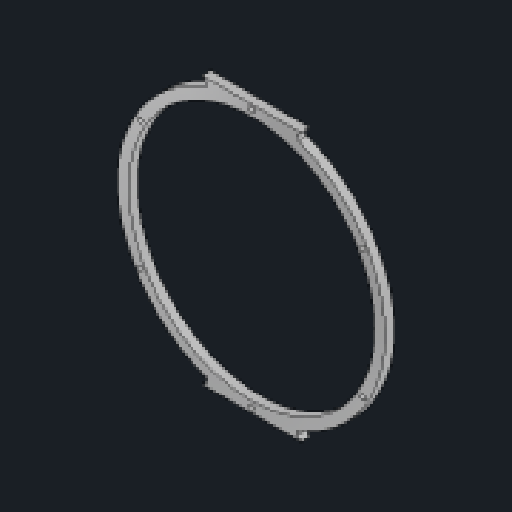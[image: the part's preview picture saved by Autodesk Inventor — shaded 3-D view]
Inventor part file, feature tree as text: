
AUTODESK INVENTOR PART (.ipt)
format: ipt  version: 2023.2 (Build 272271030, 271C)  size: 153,600 bytes
history: native  units: mm
features: extrude x4, sketch x3, mirror x2, fillet x1, pattern_circular x1
ambient origin geometry x8: Origin, YZ Plane, XZ Plane, XY Plane, X Axis, Y Axis, Z Axis, Center Point
bodies: Solid1 (feature_tree)
feature tree (11):
  sketch  "Sketch1"  dims[d0=138.0mm d1=150.0mm]
  extrude  "Extrusion1"  Depth=150.0mm
  extrude  "Extrusion2"  Depth=1.6mm
  mirror  "Mirror1"
  mirror  "Mirror2"
  extrude  "Extrusion3"  Depth=5.0mm TaperAngle=0.0deg
  extrude  "Extrusion4"  Depth=5.0mm TaperAngle=0.0deg
  fillet  "Fillet1"  Radius=3.0mm
  pattern_circular  "Circular Pattern1"  [2 undecoded]
  sketch  "Sketch2"  dims[d2=5.0mm d3=1.6mm]
  sketch  "Sketch3"  dims[d4=20.0mm d6=360.0deg d8=5.0mm d9=0.0mm d10=5.0mm d11=0.0mm d12=3.0mm d15=5.0mm d16=0.0mm d17=5.0mm d18=0.0mm d19=4.0mm d20=60.0mm d21=360.0deg d23=5.5mm]
note: 2 required parameter values undecoded (feature->parameter linkage not recoverable at this tier; creation-order binding heuristic only, values carry confidence <= 0.55)
